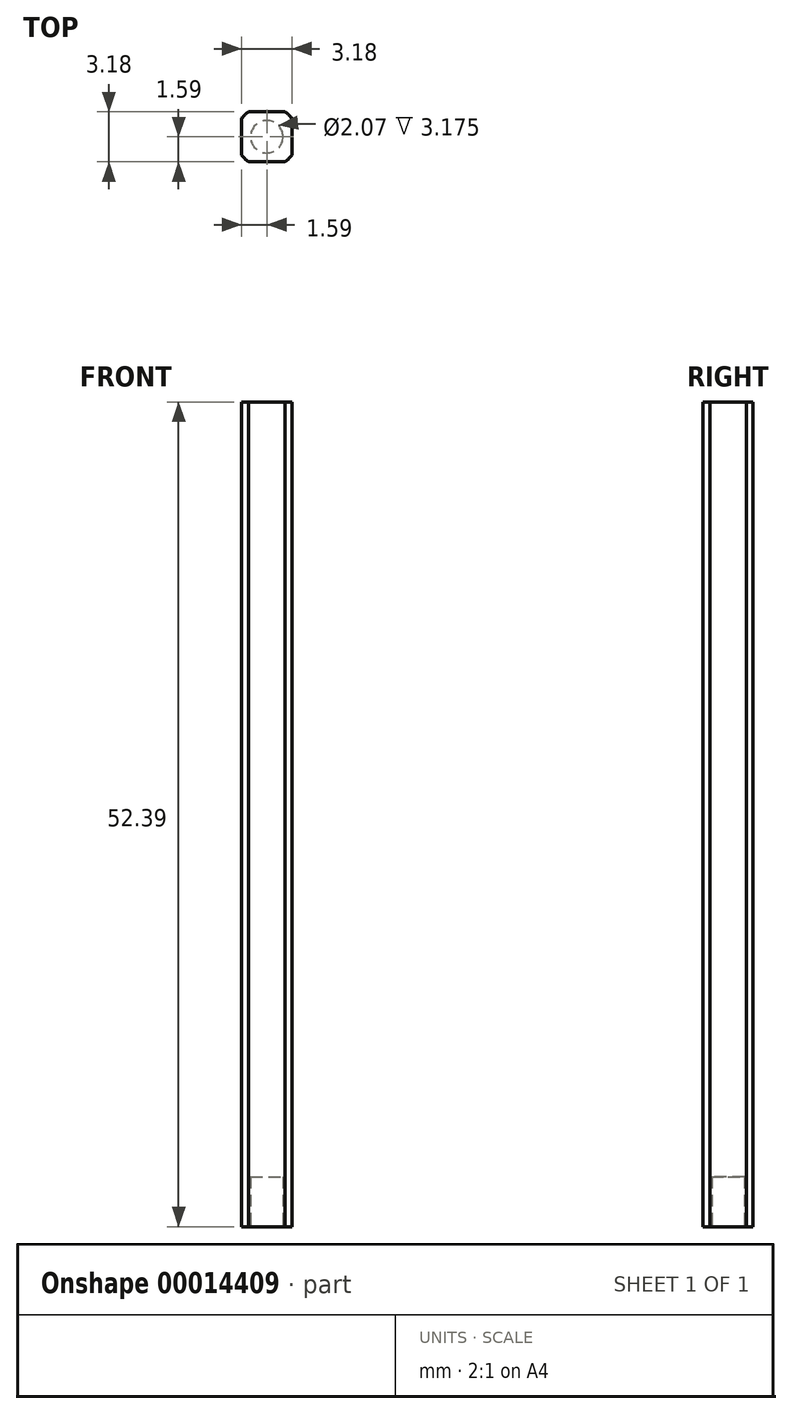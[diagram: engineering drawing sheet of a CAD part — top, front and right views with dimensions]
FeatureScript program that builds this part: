
annotation { "Feature Type Name" : "Feature", "Feature Type Description" : "" }
export const myFeature = defineFeature(function(context is Context, id is Id, definition is map)
    precondition{}
    {
        {
            var Q0;
            Q0=qCreatedBy(makeId("Top.planeOp"),FACE);
            var sketch = newSketch(context, id + "F0", { "sketchPlane" : qUnion([Q0])});
            skLineSegment(sketch, "E0.rect.bottom", {"start": v(1.16, 1.59) * mm, "end": v(-1.16, 1.59) * mm});
            skLineSegment(sketch, "E0.rect.top", {"start": v(1.16, -1.59) * mm, "end": v(-1.16, -1.59) * mm});
            skLineSegment(sketch, "E0.rect.left", {"start": v(1.59, 1.16) * mm, "end": v(1.59, -1.16) * mm});
            skLineSegment(sketch, "E0.rect.right", {"start": v(-1.59, 1.16) * mm, "end": v(-1.59, -1.16) * mm});
            skPoint(sketch, "E0.rect.middle", {"position": v(0, 0) * mm});
            skArc(sketch, "E1", {"start": v(-1.16, 1.59) * mm, "mid": v(-1.4, 1.4) * mm, "end": v(-1.59, 1.16) * mm});
            skPoint(sketch, "E2.orphan", {"position": v(1.59, 1.59) * mm});
            skPoint(sketch, "E3.orphan", {"position": v(-1.59, 1.59) * mm});
            skArc(sketch, "E4.trimOffspring", {"start": v(-1.59, -1.16) * mm, "mid": v(-1.4, -1.4) * mm, "end": v(-1.16, -1.59) * mm});
            skPoint(sketch, "E5.orphan", {"position": v(-1.59, -1.59) * mm});
            skArc(sketch, "E6.trimOffspring", {"start": v(1.16, -1.59) * mm, "mid": v(1.4, -1.4) * mm, "end": v(1.59, -1.16) * mm});
            skPoint(sketch, "E7.orphan", {"position": v(1.59, -1.59) * mm});
            skArc(sketch, "E8.trimOffspring", {"start": v(1.59, 1.16) * mm, "mid": v(1.4, 1.4) * mm, "end": v(1.16, 1.59) * mm});
            skSolve(sketch);
        }
        {
            var Q0;
            Q0=qSketchRegion(id+"F0",true);
            extrude(context, id + "F1", {"entities" : qUnion([Q0]), "depth" : 52.4 * mm});
        }
        {
            var Q0;
            Q0=makeQuery(id+"F1.opExtrude","CAP_FACE",FACE,{"disambiguationData":[OSD([sQuery(id+"F0.wireOp",EDGE,"E0.rect.bottom"),sQuery(id+"F0.wireOp",EDGE,"E0.rect.top"),sQuery(id+"F0.wireOp",EDGE,"E0.rect.left"),sQuery(id+"F0.wireOp",EDGE,"E0.rect.right"),sQuery(id+"F0.wireOp",EDGE,"E1"),sQuery(id+"F0.wireOp",EDGE,"E4.trimOffspring"),sQuery(id+"F0.wireOp",EDGE,"E6.trimOffspring"),sQuery(id+"F0.wireOp",EDGE,"E8.trimOffspring")])],"isStart":true});
            var sketch = newSketch(context, id + "F2", { "sketchPlane" : qUnion([Q0])});
            skCircle(sketch, "E9", {"center": v(0, 0) * mm, "radius": 1.03 * mm});
            skSolve(sketch);
        }
        {
            var Q0;
            Q0=qSketchRegion(id+"F2",true);
            extrude(context, id + "F3", {"entities" : qUnion([Q0]), "operationType" : NewBodyOperationType.REMOVE, "oppositeDirection" : true, "depth" : 3.17 * mm});
        }
    });
